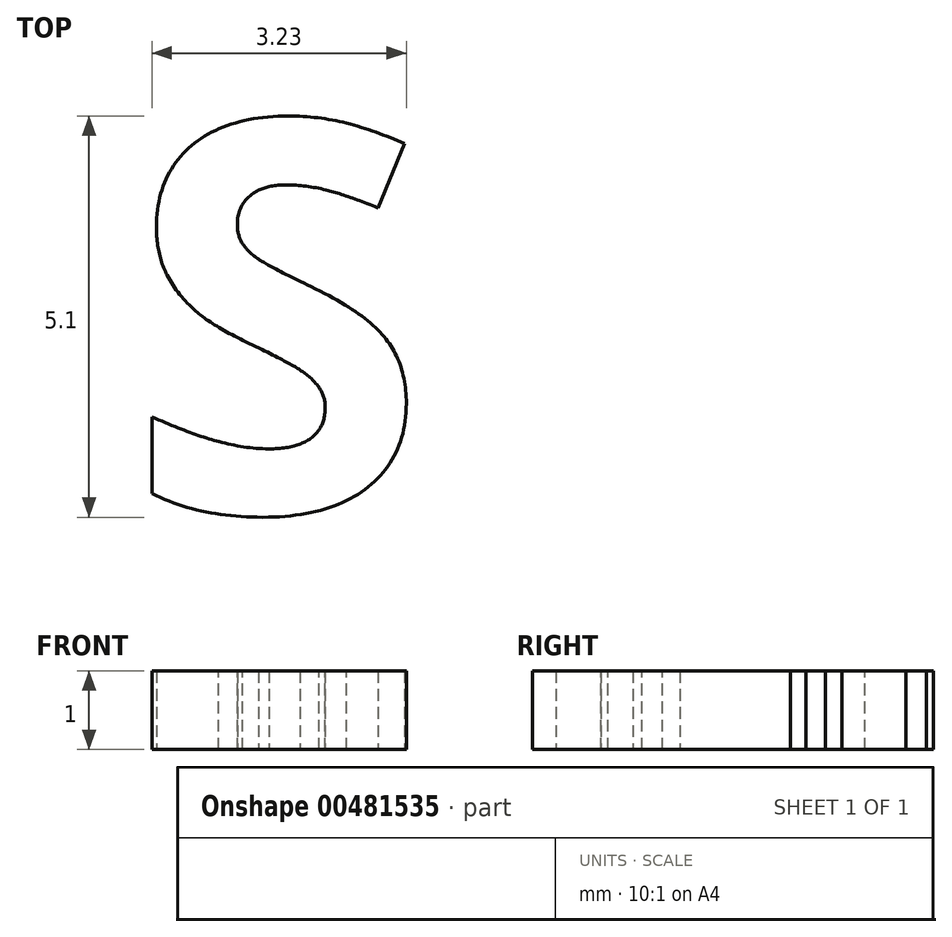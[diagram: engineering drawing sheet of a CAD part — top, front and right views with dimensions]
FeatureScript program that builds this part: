
annotation { "Feature Type Name" : "Feature", "Feature Type Description" : "" }
export const myFeature = defineFeature(function(context is Context, id is Id, definition is map)
    precondition{}
    {
        {
            var Q0;
            Q0=qCreatedBy(makeId("Top.planeOp"),FACE);
            var sketch = newSketch(context, id + "F0", { "sketchPlane" : qUnion([Q0])});
            skText(sketch, "E0", { "text": "S", "fontName": "OpenSans-Bold.ttf"});
            const initialGuessF0  = {"E0": [-0.02155, -0.0013, 1, 0, 0.005]};
            skSetInitialGuess(sketch, initialGuessF0);
            skSolve(sketch);
        }
        {
            var Q0;
            Q0 = qSketchRegion(id + "F0", true);
            extrude(context, id + "F1", {"entities" : qUnion([Q0]), "depth" : 1 * mm});
        }
    });
